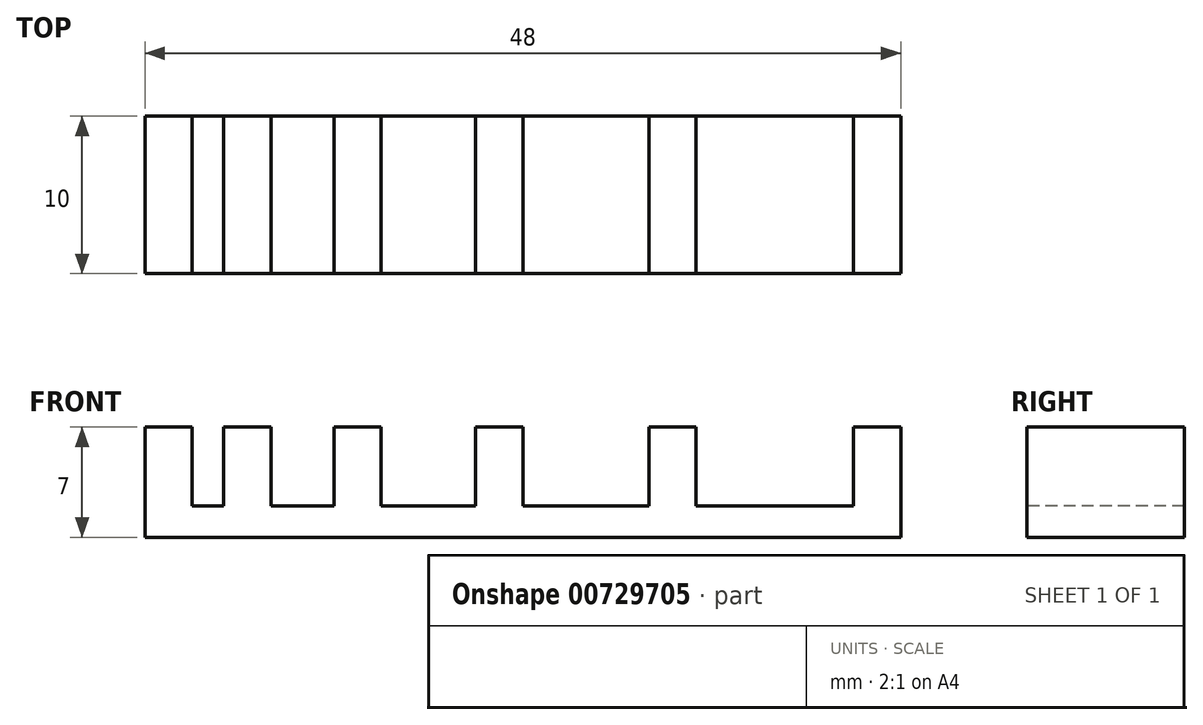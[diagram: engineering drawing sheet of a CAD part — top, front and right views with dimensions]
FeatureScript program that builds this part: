
annotation { "Feature Type Name" : "Feature", "Feature Type Description" : "" }
export const myFeature = defineFeature(function(context is Context, id is Id, definition is map)
    precondition{}
    {
        {
            var Q0;
            Q0=qCreatedBy(makeId("Top.planeOp"),FACE);
            var sketch = newSketch(context, id + "F0", { "sketchPlane" : qUnion([Q0])});
            skLineSegment(sketch, "E0.bottom", {"start": v(-28.46, 0) * mm, "end": v(-25.46, 0) * mm});
            skLineSegment(sketch, "E0.top", {"start": v(-28.46, -10) * mm, "end": v(-25.46, -10) * mm});
            skLineSegment(sketch, "E0.left", {"start": v(-28.46, 0) * mm, "end": v(-28.46, -10) * mm});
            skLineSegment(sketch, "E0.right", {"start": v(-25.46, 0) * mm, "end": v(-25.46, -10) * mm});
            skLineSegment(sketch, "E1.bottom", {"start": v(-23.46, 0) * mm, "end": v(-20.46, 0) * mm});
            skLineSegment(sketch, "E1.top", {"start": v(-23.46, -10) * mm, "end": v(-20.46, -10) * mm});
            skLineSegment(sketch, "E1.left", {"start": v(-23.46, 0) * mm, "end": v(-23.46, -10) * mm});
            skLineSegment(sketch, "E1.right", {"start": v(-20.46, 0) * mm, "end": v(-20.46, -10) * mm});
            skLineSegment(sketch, "E2.bottom", {"start": v(-16.46, 0) * mm, "end": v(-13.46, 0) * mm});
            skLineSegment(sketch, "E2.top", {"start": v(-16.46, -10) * mm, "end": v(-13.46, -10) * mm});
            skLineSegment(sketch, "E2.left", {"start": v(-16.46, 0) * mm, "end": v(-16.46, -10) * mm});
            skLineSegment(sketch, "E2.right", {"start": v(-13.46, 0) * mm, "end": v(-13.46, -10) * mm});
            skLineSegment(sketch, "E3.bottom", {"start": v(-7.46, 0) * mm, "end": v(-4.46, 0) * mm});
            skLineSegment(sketch, "E3.top", {"start": v(-7.46, -10) * mm, "end": v(-4.46, -10) * mm});
            skLineSegment(sketch, "E3.left", {"start": v(-7.46, 0) * mm, "end": v(-7.46, -10) * mm});
            skLineSegment(sketch, "E3.right", {"start": v(-4.46, 0) * mm, "end": v(-4.46, -10) * mm});
            skLineSegment(sketch, "E4.bottom", {"start": v(3.54, 0) * mm, "end": v(6.54, 0) * mm});
            skLineSegment(sketch, "E4.top", {"start": v(3.54, -10) * mm, "end": v(6.54, -10) * mm});
            skLineSegment(sketch, "E4.left", {"start": v(3.54, 0) * mm, "end": v(3.54, -10) * mm});
            skLineSegment(sketch, "E4.right", {"start": v(6.54, 0) * mm, "end": v(6.54, -10) * mm});
            skLineSegment(sketch, "E5.bottom", {"start": v(16.54, 0) * mm, "end": v(19.54, 0) * mm});
            skLineSegment(sketch, "E5.top", {"start": v(16.54, -10) * mm, "end": v(19.54, -10) * mm});
            skLineSegment(sketch, "E5.left", {"start": v(16.54, 0) * mm, "end": v(16.54, -10) * mm});
            skLineSegment(sketch, "E5.right", {"start": v(19.54, 0) * mm, "end": v(19.54, -10) * mm});
            skSolve(sketch);
        }
        {
            var Q0;
            Q0 = qSketchRegion(id + "F0", true);
            extrude(context, id + "F1", {"entities" : qUnion([Q0]), "depth" : 5 * mm, "offsetDistance" : 25 * mm});
        }
        {
            var Q0;
            Q0=makeQuery(id+"F1.opExtrude","CAP_FACE",FACE,{"disambiguationData":[OSD([sQuery(id+"F0.wireOp",EDGE,"E0.bottom"),sQuery(id+"F0.wireOp",EDGE,"E0.top"),sQuery(id+"F0.wireOp",EDGE,"E0.left"),sQuery(id+"F0.wireOp",EDGE,"E0.right")])],"isStart":true});
            var sketch = newSketch(context, id + "F2", { "sketchPlane" : qUnion([Q0])});
            skPoint(sketch, "E6.0", {"position": v(19.54, 0) * mm});
            skLineSegment(sketch, "E7.bottom", {"start": v(-28.46, 10) * mm, "end": v(19.54, 10) * mm});
            skLineSegment(sketch, "E7.top", {"start": v(-28.46, 0) * mm, "end": v(19.54, 0) * mm});
            skLineSegment(sketch, "E7.left", {"start": v(-28.46, 10) * mm, "end": v(-28.46, 0) * mm});
            skLineSegment(sketch, "E7.right", {"start": v(19.54, 10) * mm, "end": v(19.54, 0) * mm});
            skSolve(sketch);
        }
        {
            var Q0;
            {var subQ2=sQuery(id+"F2.wireOp",EDGE,"E7.right");Q0=makeQuery(id+"F2.imprint","IMPRINT",FACE,{"disambiguationData":[TD([[makeQuery(id+"F2.imprint","IMPRINT",EDGE,{"derivedFrom":subQ2}),-1.0]])]});}
            var Q1;
            {var subQ0=sQuery(id+"F2.wireOp",EDGE,"E7.left");Q1=makeQuery(id+"F2.imprint","IMPRINT",FACE,{"disambiguationData":[TD([[makeQuery(id+"F2.imprint","IMPRINT",EDGE,{"derivedFrom":subQ0}),-1.0]])]});}
            extrude(context, id + "F3", {"entities" : qUnion([Q0, Q1]), "operationType" : NewBodyOperationType.ADD, "depth" : 2 * mm, "offsetDistance" : 25 * mm});
        }
    });
